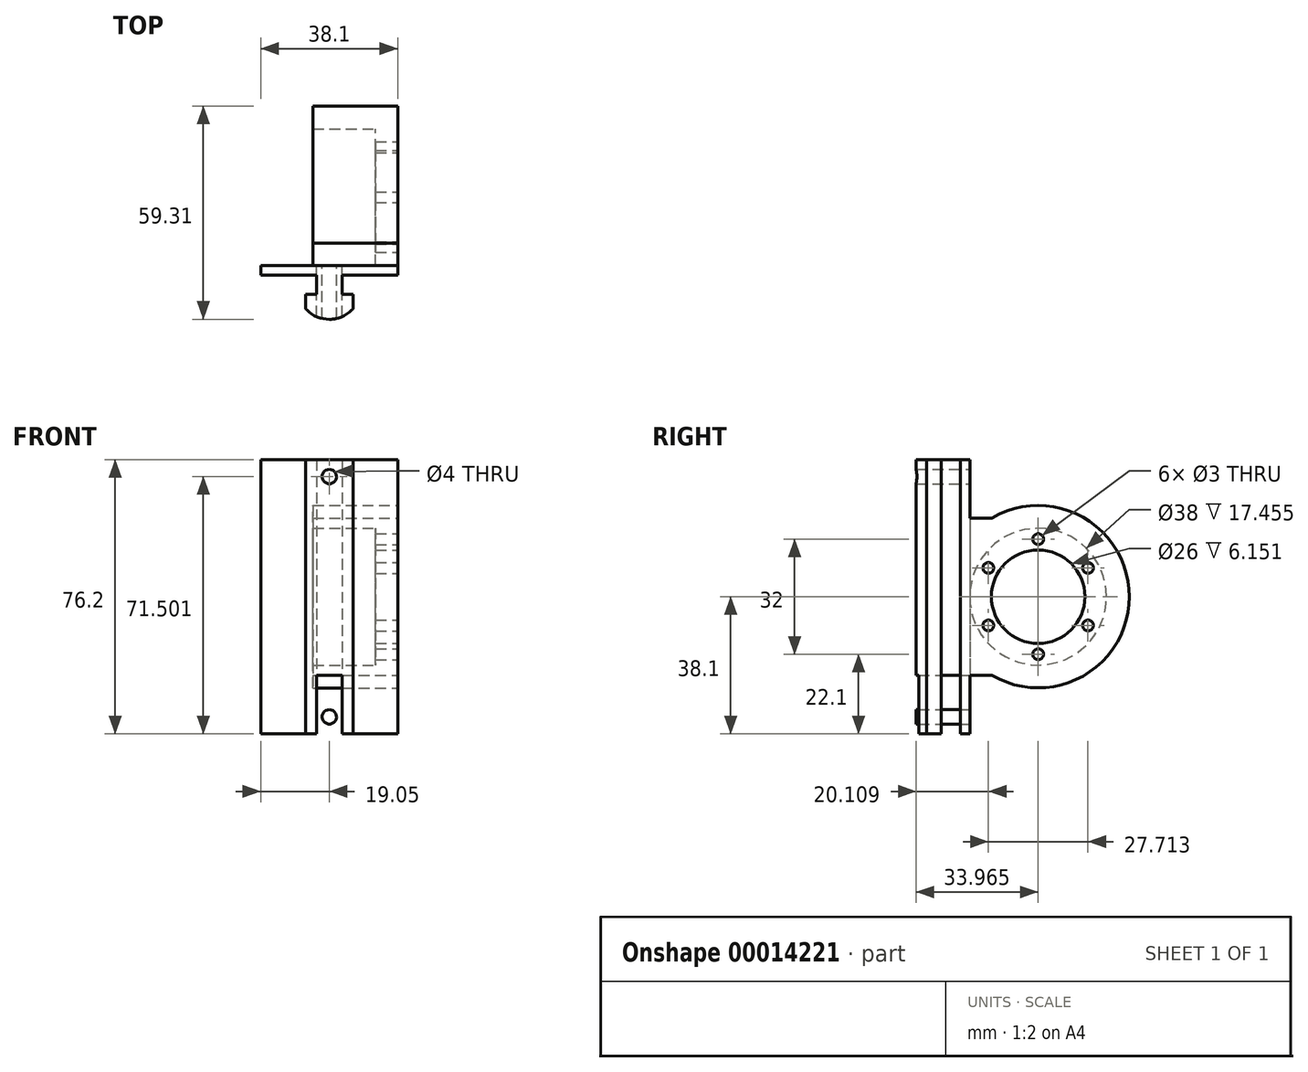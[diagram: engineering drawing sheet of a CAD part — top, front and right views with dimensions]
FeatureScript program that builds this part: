
annotation { "Feature Type Name" : "Feature", "Feature Type Description" : "" }
export const myFeature = defineFeature(function(context is Context, id is Id, definition is map)
    precondition{}
    {
        {
            var Q0;
            Q0=qCreatedBy(makeId("Top.planeOp"),FACE);
            var sketch = newSketch(context, id + "F0", { "sketchPlane" : qUnion([Q0])});
            skCircle(sketch, "E0", {"center": v(0, 0) * mm, "radius": 3.33 * mm});
            skLineSegment(sketch, "E1.bottom", {"start": v(-6.76, 6.76) * mm, "end": v(6.76, 6.76) * mm, "construction": true});
            skLineSegment(sketch, "E1.top", {"start": v(-6.76, -6.76) * mm, "end": v(6.76, -6.76) * mm, "construction": true});
            skLineSegment(sketch, "E1.left", {"start": v(-6.76, 6.76) * mm, "end": v(-6.76, -6.76) * mm, "construction": true});
            skLineSegment(sketch, "E1.right", {"start": v(6.76, 6.76) * mm, "end": v(6.76, -6.76) * mm, "construction": true});
            skLineSegment(sketch, "E2", {"start": v(-6.76, 6.76) * mm, "end": v(6.76, -6.76) * mm, "construction": true});
            skLineSegment(sketch, "E3", {"start": v(6.76, 6.76) * mm, "end": v(-6.76, -6.76) * mm, "construction": true});
            skLineSegment(sketch, "E4.bottom", {"start": v(-19.05, 19.05) * mm, "end": v(19.05, 19.05) * mm, "construction": true});
            skLineSegment(sketch, "E4.top", {"start": v(-19.05, -19.05) * mm, "end": v(19.05, -19.05) * mm, "construction": true});
            skLineSegment(sketch, "E4.left", {"start": v(-19.05, 19.05) * mm, "end": v(-19.05, 4.06) * mm});
            skLineSegment(sketch, "E4.right", {"start": v(19.05, 19.05) * mm, "end": v(19.05, -19.05) * mm, "construction": true});
            skLineSegment(sketch, "E5", {"start": v(-19.05, 19.05) * mm, "end": v(19.05, -19.05) * mm, "construction": true});
            skLineSegment(sketch, "E6.bottom", {"start": v(-14.76, 14.76) * mm, "end": v(-4.06, 14.76) * mm});
            skLineSegment(sketch, "E6.top", {"start": v(-14.76, -14.76) * mm, "end": v(14.76, -14.76) * mm, "construction": true});
            skLineSegment(sketch, "E6.left", {"start": v(-14.76, 14.76) * mm, "end": v(-14.76, 4.06) * mm});
            skLineSegment(sketch, "E6.right", {"start": v(14.76, 14.76) * mm, "end": v(14.76, -14.76) * mm, "construction": true});
            skLineSegment(sketch, "E7", {"start": v(-19.05, 19.05) * mm, "end": v(-6.76, 6.76) * mm, "construction": true});
            skLineSegment(sketch, "E8.0", {"start": v(-19.05, 16.18) * mm, "end": v(-14.76, 11.88) * mm, "construction": true});
            skLineSegment(sketch, "E9.0.MirrorCS", {"start": v(-16.18, 19.05) * mm, "end": v(-11.88, 14.76) * mm, "construction": true});
            skLineSegment(sketch, "E10", {"start": v(-11.88, 14.76) * mm, "end": v(-6.63, 9.5) * mm});
            skLineSegment(sketch, "E11", {"start": v(-14.76, 11.88) * mm, "end": v(-9.5, 6.63) * mm});
            skLineSegment(sketch, "E12", {"start": v(11.88, -14.76) * mm, "end": v(16.18, -19.05) * mm, "construction": true});
            skLineSegment(sketch, "E13", {"start": v(14.76, -11.88) * mm, "end": v(19.05, -16.18) * mm, "construction": true});
            skLineSegment(sketch, "E14.0", {"start": v(11.88, 14.76) * mm, "end": v(6.63, 9.5) * mm});
            skLineSegment(sketch, "E15.0.MirrorCS", {"start": v(14.76, 11.88) * mm, "end": v(9.5, 6.63) * mm});
            skLineSegment(sketch, "E16", {"start": v(-6.76, 3.88) * mm, "end": v(3.88, -6.76) * mm, "construction": true});
            skLineSegment(sketch, "E17", {"start": v(-3.88, 6.76) * mm, "end": v(6.76, -3.88) * mm, "construction": true});
            skLineSegment(sketch, "E18", {"start": v(3.88, 6.76) * mm, "end": v(-6.76, -3.88) * mm, "construction": true});
            skLineSegment(sketch, "E19", {"start": v(6.76, 3.88) * mm, "end": v(-3.88, -6.76) * mm, "construction": true});
            skLineSegment(sketch, "E20", {"start": v(6.76, -3.88) * mm, "end": v(9.5, -6.63) * mm, "construction": true});
            skLineSegment(sketch, "E21", {"start": v(3.88, -6.76) * mm, "end": v(6.63, -9.5) * mm, "construction": true});
            skLineSegment(sketch, "E22", {"start": v(-3.88, -6.76) * mm, "end": v(-6.63, -9.5) * mm, "construction": true});
            skLineSegment(sketch, "E23", {"start": v(-6.76, -3.88) * mm, "end": v(-9.5, -6.63) * mm, "construction": true});
            skLineSegment(sketch, "E24", {"start": v(-6.76, 3.88) * mm, "end": v(-6.76, -3.88) * mm, "construction": true});
            skLineSegment(sketch, "E25", {"start": v(-3.88, -6.76) * mm, "end": v(3.88, -6.76) * mm, "construction": true});
            skLineSegment(sketch, "E26", {"start": v(6.76, -3.88) * mm, "end": v(6.76, 3.88) * mm, "construction": true});
            skLineSegment(sketch, "E27", {"start": v(3.88, 6.76) * mm, "end": v(-3.88, 6.76) * mm, "construction": true});
            skArc(sketch, "E28", {"start": v(-6.63, 9.5) * mm, "mid": v(0, 6.76) * mm, "end": v(6.63, 9.5) * mm});
            skLineSegment(sketch, "E29", {"start": v(-6.63, 9.5) * mm, "end": v(-3.88, 6.76) * mm, "construction": true});
            skLineSegment(sketch, "E30", {"start": v(6.63, 9.5) * mm, "end": v(3.88, 6.76) * mm, "construction": true});
            skArc(sketch, "E31", {"start": v(9.5, 6.63) * mm, "mid": v(6.76, 0) * mm, "end": v(9.5, -6.63) * mm});
            skLineSegment(sketch, "E32", {"start": v(6.63, -9.5) * mm, "end": v(6.63, -9.5) * mm});
            skArc(sketch, "E33", {"start": v(-9.5, -6.63) * mm, "mid": v(-6.76, 0) * mm, "end": v(-9.5, 6.63) * mm});
            skLineSegment(sketch, "E34", {"start": v(-9.5, 6.63) * mm, "end": v(-6.76, 3.88) * mm, "construction": true});
            skLineSegment(sketch, "E35", {"start": v(-9.5, -6.63) * mm, "end": v(-14.76, -11.88) * mm});
            skLineSegment(sketch, "E36", {"start": v(-6.63, -9.5) * mm, "end": v(-11.88, -14.76) * mm});
            skLineSegment(sketch, "E37", {"start": v(9.5, -6.63) * mm, "end": v(14.76, -11.88) * mm});
            skLineSegment(sketch, "E38", {"start": v(9.5, 6.63) * mm, "end": v(6.76, 3.88) * mm, "construction": true});
            skArc(sketch, "E39", {"start": v(6.63, -9.5) * mm, "mid": v(0, -6.76) * mm, "end": v(-6.63, -9.5) * mm});
            skLineSegment(sketch, "E40", {"start": v(6.63, -9.5) * mm, "end": v(11.88, -14.76) * mm});
            skLineSegment(sketch, "E41", {"start": v(0, 0) * mm, "end": v(-19.05, 0) * mm, "construction": true});
            skLineSegment(sketch, "E42", {"start": v(-19.05, 0) * mm, "end": v(-14.76, 0) * mm, "construction": true});
            skLineSegment(sketch, "E43.0", {"start": v(-19.05, -4.06) * mm, "end": v(-14.76, -4.06) * mm});
            skLineSegment(sketch, "E44.0.MirrorCS", {"start": v(-19.05, 4.06) * mm, "end": v(-14.76, 4.06) * mm});
            skLineSegment(sketch, "E45", {"start": v(0, 0) * mm, "end": v(0, 19.05) * mm, "construction": true});
            skLineSegment(sketch, "E46", {"start": v(0, 0) * mm, "end": v(19.05, 0) * mm, "construction": true});
            skLineSegment(sketch, "E47", {"start": v(0, 0) * mm, "end": v(0, -19.05) * mm, "construction": true});
            skLineSegment(sketch, "E48.1.0", {"start": v(-4.06, -19.05) * mm, "end": v(-4.06, -14.76) * mm});
            skLineSegment(sketch, "E48.1.1", {"start": v(4.06, -19.05) * mm, "end": v(4.06, -14.76) * mm});
            skLineSegment(sketch, "E48.2.0", {"start": v(19.05, -4.06) * mm, "end": v(14.76, -4.06) * mm});
            skLineSegment(sketch, "E48.2.1", {"start": v(19.05, 4.06) * mm, "end": v(14.76, 4.06) * mm});
            skLineSegment(sketch, "E48.3.0", {"start": v(4.06, 19.05) * mm, "end": v(4.06, 14.76) * mm});
            skLineSegment(sketch, "E48.3.1", {"start": v(-4.06, 19.05) * mm, "end": v(-4.06, 14.76) * mm});
            skLineSegment(sketch, "E49", {"start": v(-14.76, 4.06) * mm, "end": v(-14.76, -4.06) * mm, "construction": true});
            skLineSegment(sketch, "E50", {"start": v(-14.76, -4.06) * mm, "end": v(-14.76, -14.76) * mm});
            skLineSegment(sketch, "E51", {"start": v(-19.05, -4.06) * mm, "end": v(-19.05, -19.05) * mm});
            skLineSegment(sketch, "E52", {"start": v(-19.05, 4.06) * mm, "end": v(-19.05, -4.06) * mm, "construction": true});
            skLineSegment(sketch, "E53", {"start": v(-4.06, 14.76) * mm, "end": v(4.06, 14.76) * mm, "construction": true});
            skLineSegment(sketch, "E54", {"start": v(4.06, 14.76) * mm, "end": v(14.76, 14.76) * mm});
            skLineSegment(sketch, "E55", {"start": v(-19.05, 19.05) * mm, "end": v(-4.06, 19.05) * mm});
            skLineSegment(sketch, "E56", {"start": v(4.06, 19.05) * mm, "end": v(19.05, 19.05) * mm});
            skLineSegment(sketch, "E57", {"start": v(19.05, 19.05) * mm, "end": v(19.05, 4.06) * mm});
            skLineSegment(sketch, "E58", {"start": v(19.05, -4.06) * mm, "end": v(19.05, -19.05) * mm});
            skLineSegment(sketch, "E59", {"start": v(4.06, -19.05) * mm, "end": v(19.05, -19.05) * mm});
            skLineSegment(sketch, "E60", {"start": v(-4.06, -19.05) * mm, "end": v(-19.05, -19.05) * mm});
            skLineSegment(sketch, "E61", {"start": v(14.76, 14.76) * mm, "end": v(14.76, 4.06) * mm});
            skLineSegment(sketch, "E62", {"start": v(14.76, -4.06) * mm, "end": v(14.76, -14.76) * mm});
            skLineSegment(sketch, "E63", {"start": v(4.06, -14.76) * mm, "end": v(14.76, -14.76) * mm});
            skLineSegment(sketch, "E64", {"start": v(-4.06, -14.76) * mm, "end": v(-14.76, -14.76) * mm});
            skCircle(sketch, "E65", {"center": v(-9.21, 13.65) * mm, "radius": 1.1 * mm});
            skCircle(sketch, "E66", {"center": v(9.21, 13.65) * mm, "radius": 1.1 * mm});
            skLineSegment(sketch, "E67", {"start": v(-9.21, 13.65) * mm, "end": v(-10.32, 13.65) * mm, "construction": true});
            skLineSegment(sketch, "E68", {"start": v(9.21, 13.65) * mm, "end": v(10.32, 13.65) * mm, "construction": true});
            skLineSegment(sketch, "E69", {"start": v(-6.63, 9.5) * mm, "end": v(-6.63, 14.76) * mm});
            skLineSegment(sketch, "E70", {"start": v(6.63, 9.5) * mm, "end": v(6.63, 14.76) * mm});
            skSolve(sketch);
        }
        {
            var Q0;
            Q0=makeQuery(id+"F0.imprint","IMPRINT",FACE,{"disambiguationData":[TD([[makeQuery(id+"F0.imprint","IMPRINT",EDGE,{"derivedFrom":sQuery(id+"F0.wireOp",EDGE,"E4.left")}),1.0]])]});
            var Q1;
            Q1=makeQuery(id+"F0.imprint","IMPRINT",FACE,{"disambiguationData":[TD([[makeQuery(id+"F0.imprint","IMPRINT",EDGE,{"derivedFrom":sQuery(id+"F0.wireOp",EDGE,"E0")}),-1.0]])]});
            var Q2;
            {var subQ1=sQuery(id+"F0.wireOp",EDGE,"E48.2.1");Q2=makeQuery(id+"F0.imprint","IMPRINT",FACE,{"disambiguationData":[TD([[makeQuery(id+"F0.imprint","IMPRINT",EDGE,{"derivedFrom":subQ1}),-1.0]])]});}
            var Q3;
            {var subQ5=sQuery(id+"F0.wireOp",EDGE,"E48.1.1");Q3=makeQuery(id+"F0.imprint","IMPRINT",FACE,{"disambiguationData":[TD([[makeQuery(id+"F0.imprint","IMPRINT",EDGE,{"derivedFrom":subQ5}),-1.0]])]});}
            var Q4;
            {var subQ5=sQuery(id+"F0.wireOp",EDGE,"E43.0");Q4=makeQuery(id+"F0.imprint","IMPRINT",FACE,{"disambiguationData":[TD([[makeQuery(id+"F0.imprint","IMPRINT",EDGE,{"derivedFrom":subQ5}),-1.0]])]});}
            extrude(context, id + "F1", {"entities" : qUnion([Q0, Q1, Q2, Q3, Q4]), "endBound" : BoundingType.SYMMETRIC, "depth" : 254 * mm});
        }
        {
            var Q0;
            Q0=qCreatedBy(makeId("Top.planeOp"),FACE);
            var sketch = newSketch(context, id + "F2", { "sketchPlane" : qUnion([Q0])});
            skLineSegment(sketch, "E71.0", {"start": v(-19.05, 19.05) * mm, "end": v(19.05, -19.05) * mm, "construction": true});
            skPoint(sketch, "E72.0", {"position": v(19.05, 19.05) * mm});
            skLineSegment(sketch, "E73", {"start": v(0, 0) * mm, "end": v(19.05, 19.05) * mm, "construction": true});
            skLineSegment(sketch, "E74", {"start": v(-19.05, 19.05) * mm, "end": v(0, 0) * mm});
            skLineSegment(sketch, "E75", {"start": v(19.05, 19.05) * mm, "end": v(0, 0) * mm});
            skLineSegment(sketch, "E76", {"start": v(19.05, 19.05) * mm, "end": v(-19.05, 19.05) * mm});
            skCircle(sketch, "E77.0", {"center": v(0, 0) * mm, "radius": 3.33 * mm});
            skLineSegment(sketch, "E78", {"start": v(-19.05, 19.05) * mm, "end": v(-19.05, 22.23) * mm});
            skLineSegment(sketch, "E79", {"start": v(-19.05, 22.23) * mm, "end": v(19.05, 22.23) * mm});
            skLineSegment(sketch, "E80", {"start": v(19.05, 22.23) * mm, "end": v(19.05, 19.05) * mm});
            skSolve(sketch);
        }
        {
            var Q0;
            {var subQ5=sQuery(id+"F2.wireOp",EDGE,"E76");Q0=makeQuery(id+"F2.imprint","IMPRINT",FACE,{"disambiguationData":[TD([[makeQuery(id+"F2.imprint","IMPRINT",EDGE,{"derivedFrom":subQ5}),1.0]])]});}
            var Q1;
            Q1=makeQuery(id+"F2.imprint","IMPRINT",FACE,{"disambiguationData":[TD([[makeQuery(id+"F2.imprint","IMPRINT",EDGE,{"derivedFrom":sQuery(id+"F2.wireOp",EDGE,"E76")}),-1.0]])]});
            extrude(context, id + "F3", {"entities" : qUnion([Q0, Q1]), "endBound" : BoundingType.SYMMETRIC, "depth" : 76.2 * mm});
        }
        {
            var Q0;
            Q0=makeQuery(id+"F1.opExtrude","SWEPT_BODY",BODY,{"disambiguationData":[OSD([sQuery(id+"F0.wireOp",EDGE,"E0"),sQuery(id+"F0.wireOp",EDGE,"E4.left"),sQuery(id+"F0.wireOp",EDGE,"E6.bottom"),sQuery(id+"F0.wireOp",EDGE,"E6.left"),sQuery(id+"F0.wireOp",EDGE,"E10"),sQuery(id+"F0.wireOp",EDGE,"E11"),sQuery(id+"F0.wireOp",EDGE,"E14.0"),sQuery(id+"F0.wireOp",EDGE,"E15.0.MirrorCS"),sQuery(id+"F0.wireOp",EDGE,"E28"),sQuery(id+"F0.wireOp",EDGE,"E31"),sQuery(id+"F0.wireOp",EDGE,"E33"),sQuery(id+"F0.wireOp",EDGE,"E35"),sQuery(id+"F0.wireOp",EDGE,"E36"),sQuery(id+"F0.wireOp",EDGE,"E37"),sQuery(id+"F0.wireOp",EDGE,"E39"),sQuery(id+"F0.wireOp",EDGE,"E40"),sQuery(id+"F0.wireOp",EDGE,"E43.0"),sQuery(id+"F0.wireOp",EDGE,"E44.0.MirrorCS"),sQuery(id+"F0.wireOp",EDGE,"E48.1.0"),sQuery(id+"F0.wireOp",EDGE,"E48.1.1"),sQuery(id+"F0.wireOp",EDGE,"E48.2.0"),sQuery(id+"F0.wireOp",EDGE,"E48.2.1"),sQuery(id+"F0.wireOp",EDGE,"E48.3.0"),sQuery(id+"F0.wireOp",EDGE,"E48.3.1"),sQuery(id+"F0.wireOp",EDGE,"E50"),sQuery(id+"F0.wireOp",EDGE,"E51"),sQuery(id+"F0.wireOp",EDGE,"E54"),sQuery(id+"F0.wireOp",EDGE,"E55"),sQuery(id+"F0.wireOp",EDGE,"E56"),sQuery(id+"F0.wireOp",EDGE,"E57"),sQuery(id+"F0.wireOp",EDGE,"E58"),sQuery(id+"F0.wireOp",EDGE,"E59"),sQuery(id+"F0.wireOp",EDGE,"E60"),sQuery(id+"F0.wireOp",EDGE,"E61"),sQuery(id+"F0.wireOp",EDGE,"E62"),sQuery(id+"F0.wireOp",EDGE,"E63"),sQuery(id+"F0.wireOp",EDGE,"E64")])]});
            var Q1;
            Q1=makeQuery(id+"F3.opExtrude","SWEPT_BODY",BODY,{"disambiguationData":[OSD([sQuery(id+"F2.wireOp",EDGE,"E74"),sQuery(id+"F2.wireOp",EDGE,"E75"),sQuery(id+"F2.wireOp",EDGE,"E76")])]});
            booleanBodies(context, id + "F4", {"operationType" : BooleanOperationType.SUBTRACTION, "tools" : qUnion([Q0]), "targets" : qUnion([Q1]), "offset" : true, "offsetAll" : true, "offsetDistance" : 0.5 * mm});
        }
        {
            var Q0;
            {var subQ1=sQuery(id+"F0.wireOp",EDGE,"E10");var subQ3=sQuery(id+"F0.wireOp",EDGE,"E6.bottom");var subQ5=makeQuery(id+"F0.imprint","INTERSECT",VERTEX,{"derivedFrom":[subQ3,subQ1]});Q0=makeQuery(id+"F0.imprint","IMPRINT",FACE,{"disambiguationData":[TD([[makeQuery(id+"F0.imprint","IMPRINT",EDGE,{"disambiguationData":[TD([[subQ5,-1.0]])],"derivedFrom":subQ3}),-1.0]])]});}
            var Q1;
            {var subQ0=sQuery(id+"F0.wireOp",EDGE,"E65");var subQ2=makeQuery(id+"F0.imprint","INTERSECT",VERTEX,{"derivedFrom":[sQuery(id+"F0.wireOp",EDGE,"E6.bottom"),subQ0]});Q1=makeQuery(id+"F0.imprint","IMPRINT",FACE,{"disambiguationData":[TD([[makeQuery(id+"F0.imprint","IMPRINT",EDGE,{"disambiguationData":[TD([[subQ2,-1.0]])],"derivedFrom":subQ0}),1.0]])]});}
            var Q2;
            {var subQ0=sQuery(id+"F0.wireOp",EDGE,"E69");Q2=makeQuery(id+"F0.imprint","IMPRINT",FACE,{"disambiguationData":[TD([[makeQuery(id+"F0.imprint","IMPRINT",EDGE,{"derivedFrom":subQ0}),1.0]])]});}
            var Q3;
            {var subQ0=sQuery(id+"F0.wireOp",EDGE,"E70");Q3=makeQuery(id+"F0.imprint","IMPRINT",FACE,{"disambiguationData":[TD([[makeQuery(id+"F0.imprint","IMPRINT",EDGE,{"derivedFrom":subQ0}),-1.0]])]});}
            var Q4;
            {var subQ0=sQuery(id+"F0.wireOp",EDGE,"E66");var subQ2=makeQuery(id+"F0.imprint","INTERSECT",VERTEX,{"derivedFrom":[sQuery(id+"F0.wireOp",EDGE,"E14.0"),subQ0]});Q4=makeQuery(id+"F0.imprint","IMPRINT",FACE,{"disambiguationData":[TD([[makeQuery(id+"F0.imprint","IMPRINT",EDGE,{"disambiguationData":[TD([[subQ2,1.0]])],"derivedFrom":subQ0}),1.0]])]});}
            var Q5;
            {var subQ1=sQuery(id+"F0.wireOp",EDGE,"E54");var subQ3=sQuery(id+"F0.wireOp",EDGE,"E14.0");var subQ5=makeQuery(id+"F0.imprint","INTERSECT",VERTEX,{"derivedFrom":[subQ3,subQ1]});Q5=makeQuery(id+"F0.imprint","IMPRINT",FACE,{"disambiguationData":[TD([[makeQuery(id+"F0.imprint","IMPRINT",EDGE,{"disambiguationData":[TD([[subQ5,-1.0]])],"derivedFrom":subQ3}),-1.0]])]});}
            extrude(context, id + "F5", {"entities" : qUnion([Q0, Q1, Q2, Q3, Q4, Q5]), "operationType" : NewBodyOperationType.REMOVE, "endBound" : BoundingType.SYMMETRIC, "oppositeDirection" : true, "depth" : 76.2 * mm});
        }
        {
            var Q0;
            Q0=makeQuery(id+"F3.opExtrude","SWEPT_FACE",FACE,{"disambiguationData":[OSD([sQuery(id+"F2.wireOp",EDGE,"E80")])]});
            var sketch = newSketch(context, id + "F6", { "sketchPlane" : qUnion([Q0])});
            skCircle(sketch, "E81", {"center": v(41.23, 0) * mm, "radius": 19 * mm});
            skArc(sketch, "E82.0", {"start": v(28.4, -21.86) * mm, "mid": v(66.58, 0) * mm, "end": v(28.4, 21.86) * mm});
            skLineSegment(sketch, "E83", {"start": v(22.23, 21.86) * mm, "end": v(28.4, 21.86) * mm});
            skLineSegment(sketch, "E84.0.MirrorCS", {"start": v(22.23, -21.86) * mm, "end": v(28.4, -21.86) * mm});
            skCircle(sketch, "E85.0", {"center": v(41.23, 0) * mm, "radius": 13 * mm});
            skLineSegment(sketch, "E86.bottom", {"start": v(22.23, 21.86) * mm, "end": v(21.54, 21.86) * mm});
            skLineSegment(sketch, "E86.top", {"start": v(22.23, -21.86) * mm, "end": v(21.54, -21.86) * mm});
            skLineSegment(sketch, "E86.left", {"start": v(22.23, 16.78) * mm, "end": v(22.23, -16.78) * mm});
            skLineSegment(sketch, "E86.right", {"start": v(21.54, 21.86) * mm, "end": v(21.54, -21.86) * mm});
            skCircle(sketch, "E87", {"center": v(41.23, 0) * mm, "radius": 16 * mm, "construction": true});
            skLineSegment(sketch, "E88", {"start": v(28.23, 0) * mm, "end": v(22.23, 0) * mm, "construction": true});
            skPoint(sketch, "E89", {"position": v(25.23, 0) * mm});
            skCircle(sketch, "E90", {"center": v(41.23, 16) * mm, "radius": 1.5 * mm});
            skCircle(sketch, "E91", {"center": v(27.37, 8) * mm, "radius": 1.5 * mm});
            skCircle(sketch, "E92", {"center": v(55.08, 8) * mm, "radius": 1.5 * mm});
            skLineSegment(sketch, "E93", {"start": v(27.37, 8) * mm, "end": v(41.23, 0) * mm, "construction": true});
            skLineSegment(sketch, "E94", {"start": v(41.23, 16) * mm, "end": v(41.23, 0) * mm, "construction": true});
            skLineSegment(sketch, "E95", {"start": v(41.23, 0) * mm, "end": v(55.08, 8) * mm, "construction": true});
            skLineSegment(sketch, "E96", {"start": v(22.23, 0) * mm, "end": v(66.58, 0) * mm, "construction": true});
            skCircle(sketch, "E97.MirrorC", {"center": v(27.37, -8) * mm, "radius": 1.5 * mm});
            skCircle(sketch, "E98.MirrorC", {"center": v(41.23, -16) * mm, "radius": 1.5 * mm});
            skCircle(sketch, "E99.MirrorC", {"center": v(55.08, -8) * mm, "radius": 1.5 * mm});
            skSolve(sketch);
        }
        {
            var Q0;
            {var subQ5=sQuery(id+"F6.wireOp",EDGE,"E86.bottom");Q0=makeQuery(id+"F6.imprint","IMPRINT",FACE,{"disambiguationData":[TD([[makeQuery(id+"F6.imprint","IMPRINT",EDGE,{"derivedFrom":subQ5}),1.0]])]});}
            var Q1;
            {var subQ4=sQuery(id+"F6.wireOp",EDGE,"E81");Q1=makeQuery(id+"F6.imprint","IMPRINT",FACE,{"disambiguationData":[TD([[makeQuery(id+"F6.imprint","IMPRINT",EDGE,{"derivedFrom":subQ4}),-1.0]])]});}
            extrude(context, id + "F7", {"entities" : qUnion([Q0, Q1]), "operationType" : NewBodyOperationType.ADD, "oppositeDirection" : true, "depth" : 23.6 * mm});
        }
        {
            var Q0;
            {var subQ5=sQuery(id+"F6.wireOp",EDGE,"E86.bottom");Q0=makeQuery(id+"F6.imprint","IMPRINT",FACE,{"disambiguationData":[TD([[makeQuery(id+"F6.imprint","IMPRINT",EDGE,{"derivedFrom":subQ5}),1.0]])]});}
            var Q1;
            Q1=makeQuery(id+"F6.imprint","IMPRINT",FACE,{"disambiguationData":[TD([[makeQuery(id+"F6.imprint","IMPRINT",EDGE,{"derivedFrom":sQuery(id+"F6.wireOp",EDGE,"E81")}),1.0]])]});
            extrude(context, id + "F8", {"entities" : qUnion([Q0, Q1]), "operationType" : NewBodyOperationType.ADD, "oppositeDirection" : true, "depth" : 6.15 * mm});
        }
        {
            var Q0;
            Q0=makeQuery(id+"F3.opExtrude","SWEPT_FACE",FACE,{"disambiguationData":[OSD([sQuery(id+"F2.wireOp",EDGE,"E79")])]});
            var sketch = newSketch(context, id + "F9", { "sketchPlane" : qUnion([Q0])});
            skLineSegment(sketch, "E100", {"start": v(0, 38.1) * mm, "end": v(0, -38.1) * mm, "construction": true});
            skCircle(sketch, "E101", {"center": v(0, 33.4) * mm, "radius": 2 * mm});
            skLineSegment(sketch, "E102.0", {"start": v(-3.56, 38.1) * mm, "end": v(-3.56, -38.1) * mm});
            skLineSegment(sketch, "E103.0", {"start": v(3.56, 38.1) * mm, "end": v(3.56, -38.1) * mm});
            skLineSegment(sketch, "E104.0", {"start": v(19.05, 0) * mm, "end": v(4.06, 0) * mm});
            skCircle(sketch, "E105.0.MirrorC", {"center": v(0, -33.4) * mm, "radius": 2 * mm});
            skSolve(sketch);
        }
        {
            var Q0;
            Q0=makeQuery(id+"F9.imprint","IMPRINT",FACE,{"disambiguationData":[TD([[makeQuery(id+"F9.imprint","IMPRINT",EDGE,{"derivedFrom":sQuery(id+"F9.wireOp",EDGE,"E101")}),1.0]])]});
            var Q1;
            Q1=makeQuery(id+"F9.imprint","IMPRINT",FACE,{"disambiguationData":[TD([[makeQuery(id+"F9.imprint","IMPRINT",EDGE,{"derivedFrom":sQuery(id+"F9.wireOp",EDGE,"E105.0.MirrorC")}),-1.0]])]});
            extrude(context, id + "F10", {"entities" : qUnion([Q0, Q1]), "operationType" : NewBodyOperationType.REMOVE, "oppositeDirection" : true, "depth" : 25.4 * mm});
        }
    });
